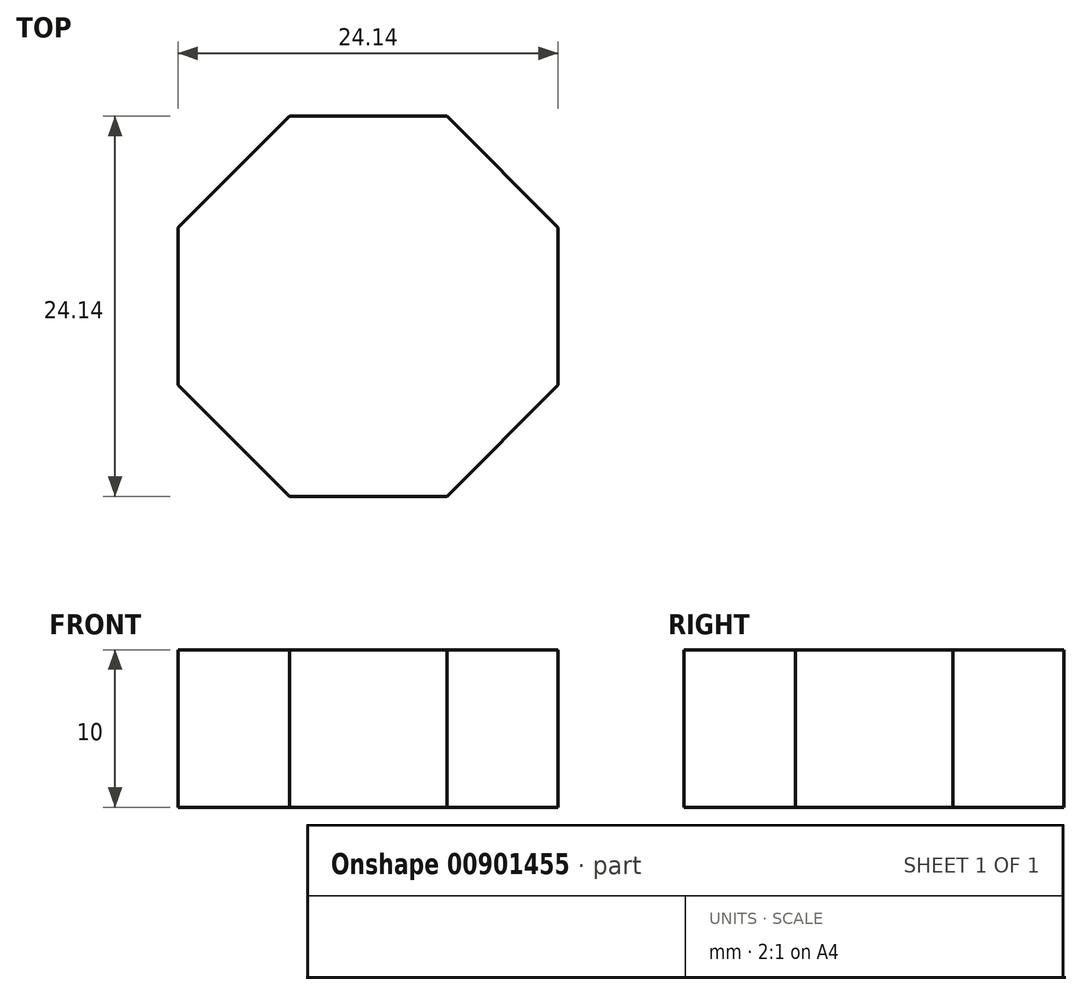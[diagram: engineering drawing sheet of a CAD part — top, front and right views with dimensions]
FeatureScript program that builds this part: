
annotation { "Feature Type Name" : "Feature", "Feature Type Description" : "" }
export const myFeature = defineFeature(function(context is Context, id is Id, definition is map)
    precondition{}
    {
        {
            var Q0;
            Q0=qCreatedBy(makeId("Top.planeOp"),FACE);
            var sketch = newSketch(context, id + "F0", { "sketchPlane" : qUnion([Q0])});
            skLineSegment(sketch, "E0", {"start": v(0, 0) * mm, "end": v(-10, 0) * mm});
            skLineSegment(sketch, "E1", {"start": v(-10, 0) * mm, "end": v(-17.07, -7.07) * mm});
            skLineSegment(sketch, "E2", {"start": v(-17.07, -7.07) * mm, "end": v(-17.07, -17.07) * mm});
            skLineSegment(sketch, "E3", {"start": v(-17.07, -17.07) * mm, "end": v(-10, -24.14) * mm});
            skLineSegment(sketch, "E4", {"start": v(-10, -24.14) * mm, "end": v(0, -24.14) * mm});
            skLineSegment(sketch, "E5", {"start": v(0, -24.14) * mm, "end": v(7.07, -17.07) * mm});
            skLineSegment(sketch, "E6", {"start": v(7.07, -17.07) * mm, "end": v(7.07, -7.07) * mm});
            skLineSegment(sketch, "E7", {"start": v(7.07, -7.07) * mm, "end": v(0, 0) * mm});
            skSolve(sketch);
        }
        {
            var Q0;
            Q0=makeQuery(id+"F0.imprint","IMPRINT",FACE,{"disambiguationData":[TD([[makeQuery(id+"F0.imprint","IMPRINT",EDGE,{"derivedFrom":sQuery(id+"F0.wireOp",EDGE,"E0")}),1.0]])]});
            extrude(context, id + "F1", {"entities" : qUnion([Q0]), "depth" : 10 * mm, "offsetDistance" : 25 * mm});
        }
    });
